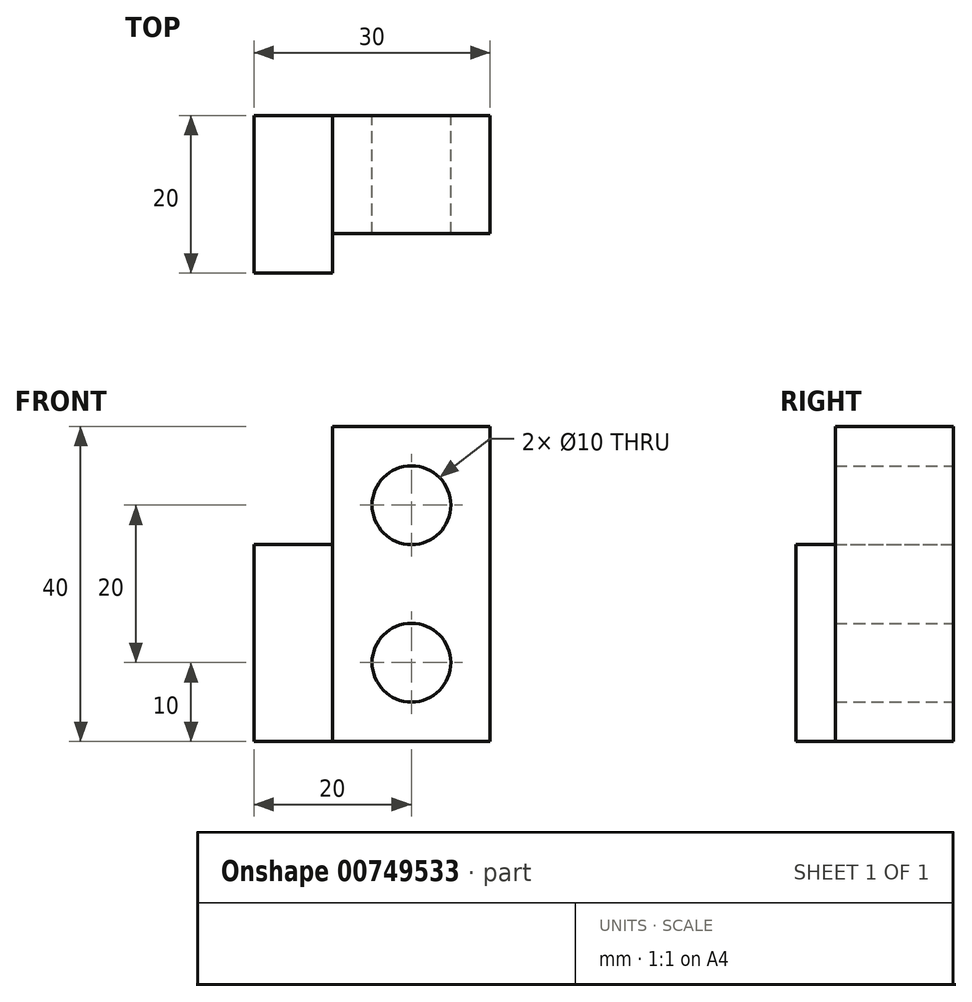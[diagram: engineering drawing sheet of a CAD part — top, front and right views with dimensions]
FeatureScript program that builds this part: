
annotation { "Feature Type Name" : "Feature", "Feature Type Description" : "" }
export const myFeature = defineFeature(function(context is Context, id is Id, definition is map)
    precondition{}
    {
        {
            var Q0;
            Q0=qCreatedBy(makeId("Front.planeOp"),FACE);
            var sketch = newSketch(context, id + "F0", { "sketchPlane" : qUnion([Q0])});
            skLineSegment(sketch, "E0", {"start": v(0, 0) * mm, "end": v(20, 0) * mm});
            skLineSegment(sketch, "E1", {"start": v(20, 0) * mm, "end": v(20, 40) * mm});
            skLineSegment(sketch, "E2", {"start": v(20, 40) * mm, "end": v(0, 40) * mm});
            skLineSegment(sketch, "E3", {"start": v(0, 40) * mm, "end": v(0, 0) * mm});
            skCircle(sketch, "E4", {"center": v(10, 10) * mm, "radius": 5 * mm});
            skCircle(sketch, "E5", {"center": v(10, 30) * mm, "radius": 5 * mm});
            skSolve(sketch);
        }
        {
            var Q0;
            Q0=makeQuery(id+"F0.imprint","IMPRINT",FACE,{"disambiguationData":[TD([[makeQuery(id+"F0.imprint","IMPRINT",EDGE,{"derivedFrom":sQuery(id+"F0.wireOp",EDGE,"E0")}),1.0]])]});
            extrude(context, id + "F1", {"entities" : qUnion([Q0]), "depth" : 15 * mm, "offsetDistance" : 25 * mm});
        }
        {
            var Q0;
            Q0=makeQuery(id+"F1.opExtrude","SWEPT_FACE",FACE,{"disambiguationData":[OSD([sQuery(id+"F0.wireOp",EDGE,"E3")])]});
            var sketch = newSketch(context, id + "F2", { "sketchPlane" : qUnion([Q0])});
            skLineSegment(sketch, "E6", {"start": v(0, 0) * mm, "end": v(20, 0) * mm});
            skLineSegment(sketch, "E7", {"start": v(20, 0) * mm, "end": v(20, 25) * mm});
            skLineSegment(sketch, "E8", {"start": v(20, 25) * mm, "end": v(0, 25) * mm});
            skLineSegment(sketch, "E9", {"start": v(0, 25) * mm, "end": v(0, 0) * mm});
            skSolve(sketch);
        }
        {
            var Q0;
            {var subQ0=sQuery(id+"F2.wireOp",EDGE,"E9");Q0=makeQuery(id+"F2.imprint","IMPRINT",FACE,{"disambiguationData":[TD([[makeQuery(id+"F2.imprint","IMPRINT",EDGE,{"derivedFrom":subQ0}),1.0]])]});}
            var Q1;
            {var subQ3=sQuery(id+"F2.wireOp",EDGE,"E7");Q1=makeQuery(id+"F2.imprint","IMPRINT",FACE,{"disambiguationData":[TD([[makeQuery(id+"F2.imprint","IMPRINT",EDGE,{"derivedFrom":subQ3}),1.0]])]});}
            extrude(context, id + "F3", {"entities" : qUnion([Q0, Q1]), "operationType" : NewBodyOperationType.ADD, "depth" : 10 * mm, "offsetDistance" : 25 * mm});
        }
    });
